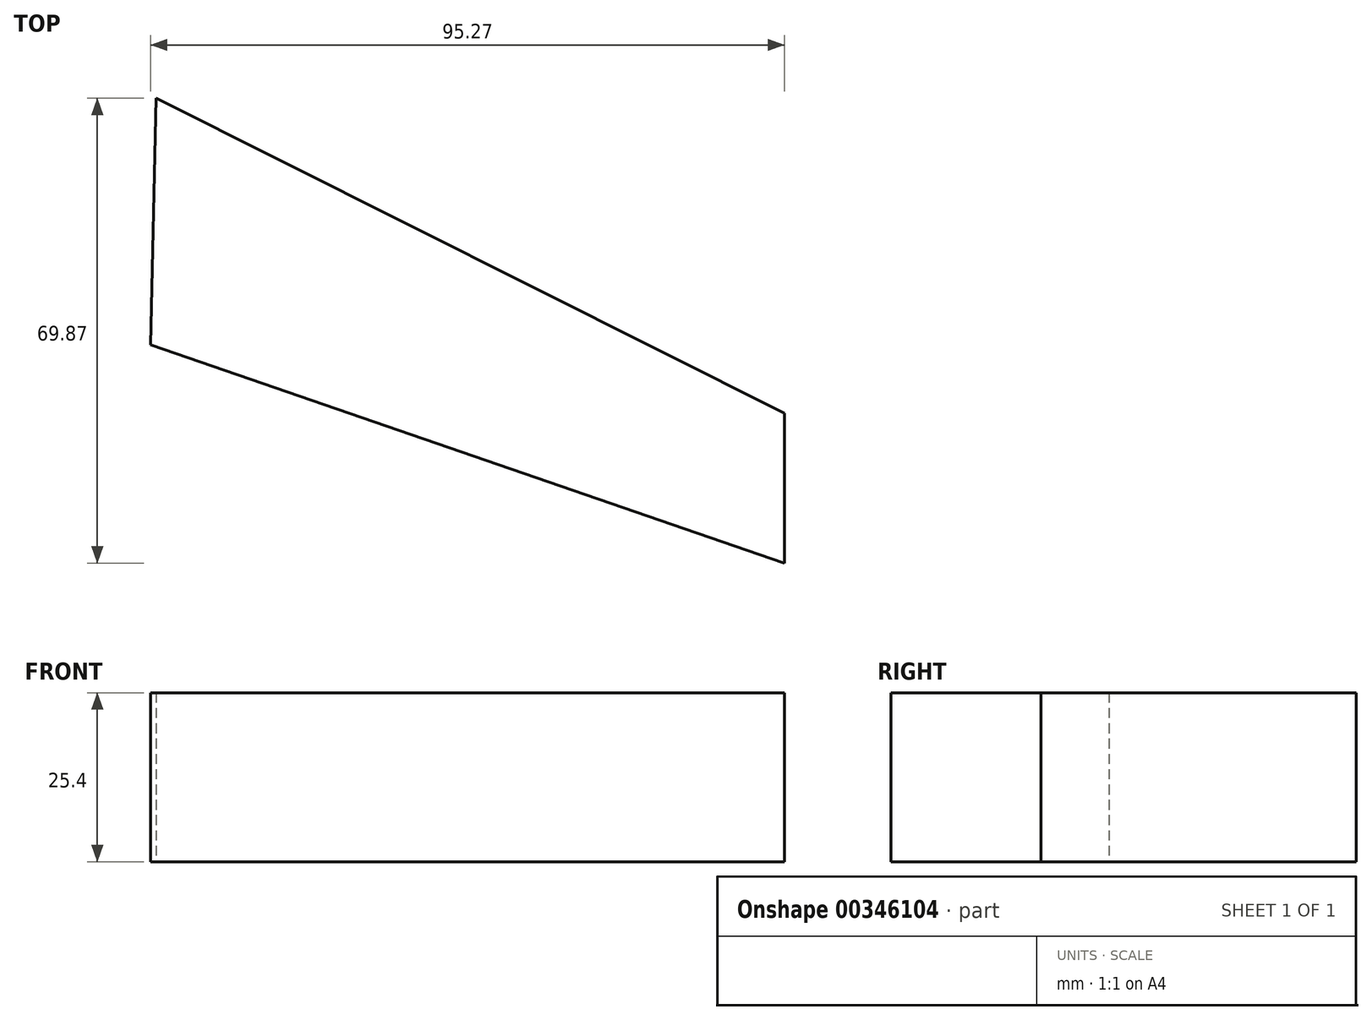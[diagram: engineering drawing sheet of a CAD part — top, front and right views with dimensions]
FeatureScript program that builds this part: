
annotation { "Feature Type Name" : "Feature", "Feature Type Description" : "" }
export const myFeature = defineFeature(function(context is Context, id is Id, definition is map)
    precondition{}
    {
        {
            var Q0;
            Q0=qCreatedBy(makeId("Top.planeOp"),FACE);
            var sketch = newSketch(context, id + "F0", { "sketchPlane" : qUnion([Q0])});
            skLineSegment(sketch, "E0", {"start": v(-19.54, -15.9) * mm, "end": v(74.9, -63.23) * mm});
            skLineSegment(sketch, "E1", {"start": v(74.9, -63.23) * mm, "end": v(74.9, -85.77) * mm});
            skLineSegment(sketch, "E2", {"start": v(74.9, -85.77) * mm, "end": v(-20.36, -53) * mm});
            skLineSegment(sketch, "E3", {"start": v(-20.36, -53) * mm, "end": v(-19.54, -15.9) * mm});
            skLineSegment(sketch, "E4", {"start": v(-17.02, -47.54) * mm, "end": v(66.37, -76.23) * mm});
            skLineSegment(sketch, "E5", {"start": v(66.37, -76.23) * mm, "end": v(66.37, -115.25) * mm});
            skLineSegment(sketch, "E6", {"start": v(64.71, -115.25) * mm, "end": v(77.38, -119.4) * mm});
            skLineSegment(sketch, "E7", {"start": v(77.38, -119.4) * mm, "end": v(74.9, -76.23) * mm});
            skLineSegment(sketch, "E8", {"start": v(66.37, -76.23) * mm, "end": v(74.9, -76.23) * mm});
            skSolve(sketch);
        }
        {
            var Q0;
            Q0 = qSketchRegion(id + "F0", true);
            extrude(context, id + "F1", {"entities" : qUnion([Q0]), "depth" : 25.4 * mm});
        }
    });
